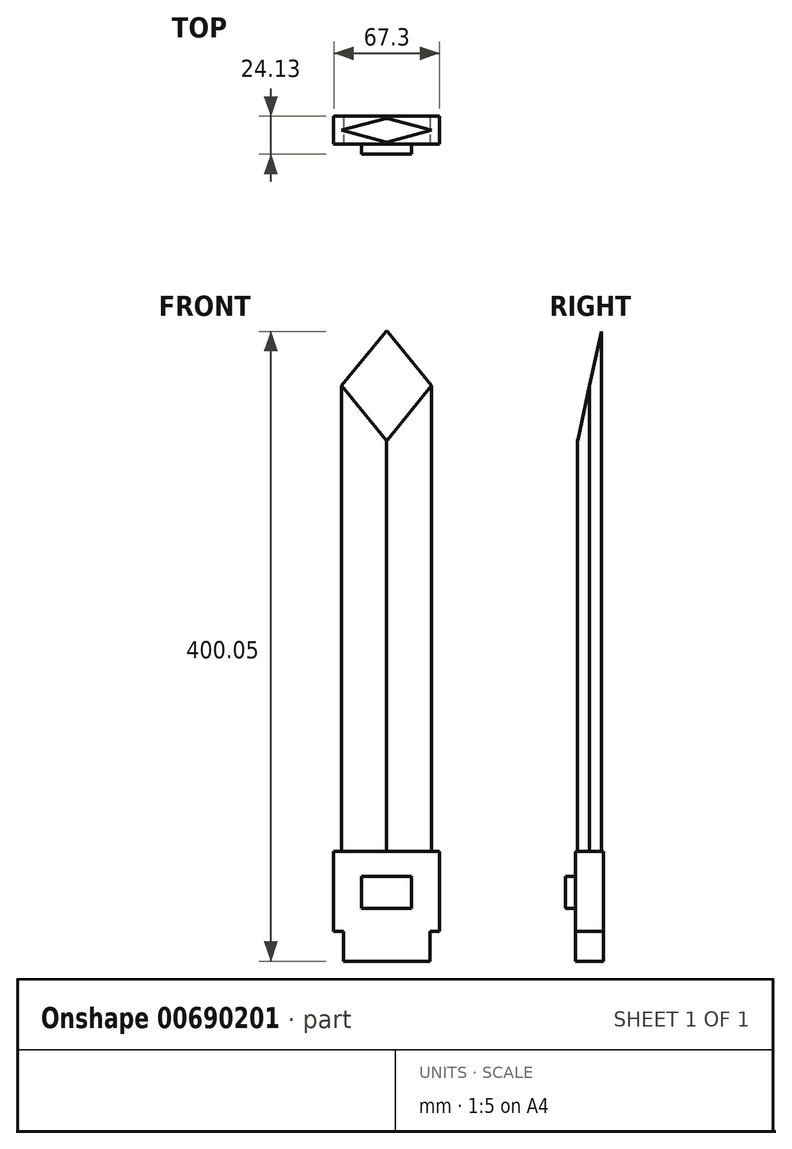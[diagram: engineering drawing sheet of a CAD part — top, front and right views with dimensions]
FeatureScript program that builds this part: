
annotation { "Feature Type Name" : "Feature", "Feature Type Description" : "" }
export const myFeature = defineFeature(function(context is Context, id is Id, definition is map)
    precondition{}
    {
        {
            var Q0;
            Q0=qCreatedBy(makeId("Top.planeOp"),FACE);
            var sketch = newSketch(context, id + "F0", { "sketchPlane" : qUnion([Q0])});
            skLineSegment(sketch, "E0", {"start": v(-28.58, 0) * mm, "end": v(28.58, 0) * mm});
            skLineSegment(sketch, "E1", {"start": v(0, -7.62) * mm, "end": v(0, 7.62) * mm});
            skLineSegment(sketch, "E2", {"start": v(-28.58, 0) * mm, "end": v(0, 7.62) * mm});
            skLineSegment(sketch, "E3", {"start": v(-28.58, 0) * mm, "end": v(0, -7.62) * mm});
            skLineSegment(sketch, "E4", {"start": v(0, 7.62) * mm, "end": v(28.58, 0) * mm});
            skLineSegment(sketch, "E5", {"start": v(0, -7.62) * mm, "end": v(28.58, 0) * mm});
            skSolve(sketch);
        }
        {
            var Q0;
            Q0 = qSketchRegion(id + "F0", true);
            extrude(context, id + "F1", {"entities" : qUnion([Q0]), "depth" : 254 * mm, "offsetDistance" : 25.4 * mm});
        }
        {
            var Q0;
            Q0=qCreatedBy(makeId("Right.planeOp"),FACE);
            var sketch = newSketch(context, id + "F2", { "sketchPlane" : qUnion([Q0])});
            skLineSegment(sketch, "E6", {"start": v(7.5, 253.98) * mm, "end": v(-7.5, 185.15) * mm});
            skSolve(sketch);
        }
        {
            var Q0;
            Q0 = qSketchRegion(id + "F2", true);
            var Q1;
            Q1=sQuery(id+"F2.wireOp",EDGE,"E6");
            extrude(context, id + "F3", {"entities" : qUnion([Q0]), "bodyType" : ToolBodyType.SURFACE, "surfaceEntities" : qUnion([Q1]), "oppositeDirection" : true, "depth" : 38.1 * mm, "offsetDistance" : 25.4 * mm});
        }
        {
            var Q0;
            Q0 = qSketchRegion(id + "F2", true);
            var Q1;
            Q1 = qConstructionFilter(qBodyType(qCreatedBy(id + "F2" ,EDGE), BodyType.WIRE), ConstructionObject.NO);
            extrude(context, id + "F4", {"entities" : qUnion([Q0]), "bodyType" : ToolBodyType.SURFACE, "surfaceOperationType" : NewSurfaceOperationType.ADD, "surfaceEntities" : qUnion([Q1]), "depth" : 44.45 * mm, "offsetDistance" : 25.4 * mm});
        }
        {
            var Q0;
            {var subQ0=sQuery(id+"F2.wireOp",EDGE,"E6");Q0=makeQuery(id+"F4.join.opBoolean","MERGE",FACE,{"derivedFrom":[makeQuery(id+"F3.opExtrude","SWEPT_FACE",FACE,{"disambiguationData":[OSD([subQ0])]}),makeQuery(id+"F4.opExtrude","SWEPT_FACE",FACE,{"disambiguationData":[OSD([subQ0])]})]});}
            extrude(context, id + "F5", {"entities" : qUnion([Q0]), "operationType" : NewBodyOperationType.REMOVE, "oppositeDirection" : true, "depth" : 25.4 * mm, "offsetDistance" : 25.4 * mm});
        }
        {
            var Q0;
            Q0=makeQuery(id+"F1.opExtrude","CAP_FACE",FACE,{"disambiguationData":[OSD([sQuery(id+"F0.wireOp",EDGE,"E2"),sQuery(id+"F0.wireOp",EDGE,"E3"),sQuery(id+"F0.wireOp",EDGE,"E4"),sQuery(id+"F0.wireOp",EDGE,"E5")])],"isStart":true});
            extrude(context, id + "F6", {"entities" : qUnion([Q0]), "operationType" : NewBodyOperationType.ADD, "depth" : 76.2 * mm, "offsetDistance" : 25.4 * mm});
        }
        {
            var Q0;
            Q0=makeQuery(id+"F6.opExtrude","CAP_FACE",FACE,{"disambiguationData":[OSD([sQuery(id+"F0.wireOp",EDGE,"E2"),sQuery(id+"F0.wireOp",EDGE,"E3"),sQuery(id+"F0.wireOp",EDGE,"E4"),sQuery(id+"F0.wireOp",EDGE,"E5")])],"isStart":false});
            var sketch = newSketch(context, id + "F7", { "sketchPlane" : qUnion([Q0])});
            skLineSegment(sketch, "E7.bottom", {"start": v(-33.66, 8.9) * mm, "end": v(33.66, 8.9) * mm});
            skLineSegment(sketch, "E7.top", {"start": v(-33.66, -8.9) * mm, "end": v(33.66, -8.9) * mm});
            skLineSegment(sketch, "E7.left", {"start": v(-33.66, 8.9) * mm, "end": v(-33.66, -8.9) * mm});
            skLineSegment(sketch, "E7.right", {"start": v(33.66, 8.9) * mm, "end": v(33.66, -8.9) * mm});
            skPoint(sketch, "E7.middle", {"position": v(0, 0) * mm});
            skSolve(sketch);
        }
        {
            var Q0;
            Q0 = qSketchRegion(id + "F7", true);
            extrude(context, id + "F8", {"entities" : qUnion([Q0]), "operationType" : NewBodyOperationType.ADD, "depth" : 50.8 * mm, "offsetDistance" : 25.4 * mm});
        }
        {
            var Q0;
            Q0=makeQuery(id+"F8.opExtrude","CAP_FACE",FACE,{"disambiguationData":[OSD([sQuery(id+"F7.wireOp",EDGE,"E7.bottom"),sQuery(id+"F7.wireOp",EDGE,"E7.top"),sQuery(id+"F7.wireOp",EDGE,"E7.left"),sQuery(id+"F7.wireOp",EDGE,"E7.right")])],"isStart":false});
            var sketch = newSketch(context, id + "F9", { "sketchPlane" : qUnion([Q0])});
            skLineSegment(sketch, "E8.bottom", {"start": v(-27.6, -8.9) * mm, "end": v(27.6, -8.9) * mm});
            skLineSegment(sketch, "E8.top", {"start": v(-27.6, 8.9) * mm, "end": v(27.6, 8.9) * mm});
            skLineSegment(sketch, "E8.left", {"start": v(-27.6, -8.9) * mm, "end": v(-27.6, 8.9) * mm});
            skLineSegment(sketch, "E8.right", {"start": v(27.6, -8.9) * mm, "end": v(27.6, 8.9) * mm});
            skPoint(sketch, "E8.middle", {"position": v(0, 0) * mm});
            skSolve(sketch);
        }
        {
            var Q0;
            Q0=makeQuery(id+"F9.imprint","IMPRINT",FACE,{"disambiguationData":[TD([[makeQuery(id+"F9.imprint","IMPRINT",EDGE,{"derivedFrom":sQuery(id+"F9.wireOp",EDGE,"E8.bottom")}),1.0]])]});
            extrude(context, id + "F10", {"entities" : qUnion([Q0]), "operationType" : NewBodyOperationType.ADD, "depth" : 19.05 * mm, "offsetDistance" : 25.4 * mm});
        }
        {
            var Q0;
            Q0=makeQuery(id+"F10.boolean.opBoolean","MERGE",FACE,{"derivedFrom":[makeQuery(id+"F8.opExtrude","SWEPT_FACE",FACE,{"disambiguationData":[OSD([sQuery(id+"F7.wireOp",EDGE,"E7.bottom")])]}),makeQuery(id+"F10.opExtrude","SWEPT_FACE",FACE,{"disambiguationData":[OSD([sQuery(id+"F9.wireOp",EDGE,"E8.top")])]})]});
            var sketch = newSketch(context, id + "F11", { "sketchPlane" : qUnion([Q0])});
            skLineSegment(sketch, "E9.bottom", {"start": v(-15.87, -112.46) * mm, "end": v(15.88, -112.46) * mm});
            skLineSegment(sketch, "E9.top", {"start": v(-15.88, -92.14) * mm, "end": v(15.88, -92.14) * mm});
            skLineSegment(sketch, "E9.left", {"start": v(-15.87, -112.46) * mm, "end": v(-15.88, -92.14) * mm});
            skLineSegment(sketch, "E9.right", {"start": v(15.88, -112.46) * mm, "end": v(15.88, -92.14) * mm});
            skPoint(sketch, "E9.middle", {"position": v(0, -102.3) * mm});
            skPoint(sketch, "E9.middle.positionSnap0", {"position": v(0, -76.2) * mm});
            skPoint(sketch, "E9.centerSnap0", {"position": v(0, -76.2) * mm});
            skSolve(sketch);
        }
        {
            var Q0;
            Q0=makeQuery(id+"F11.imprint","IMPRINT",FACE,{"disambiguationData":[TD([[makeQuery(id+"F11.imprint","IMPRINT",EDGE,{"derivedFrom":sQuery(id+"F11.wireOp",EDGE,"E9.bottom")}),1.0]])]});
            extrude(context, id + "F12", {"entities" : qUnion([Q0]), "operationType" : NewBodyOperationType.ADD, "depth" : 6.35 * mm, "offsetDistance" : 25.4 * mm});
        }
    });
